# Revit family: EdgeProtection_FloorTransition_Schluter_Deco_AE
name_source: partatom
category: Profiles
units: mm (PartAtom-declared; Revit-internal decimal feet)

## family parameters
Classification Number = 23.35.50.11.21.17
Profile Usage = <Generic>
Rotate with component = No
Section Shape = Not Defined

## types (3) — shared parameters
Assembly Code = C3020430
Construction Details = http://www.arcat.com
Description = As Specified in 09 30 00
Green Building-LEED = http://www.arcat.com
Installation-Fabrication = http://www.schluter.com
Keynote = 09 30 00
Manufacturer = Schluter System LP
Manufacturer Fax = 800-477-9783
Manufacturer Website = http://www.schluter.com
Model = As Specified in 09 30 00
Product Data = http://www.arcat.com
Product Properties = http://www.arcat.com
Sales Information = http://www.schluter.com
Send Message = http://www.arcat.com
SpecWizard = http://www.arcat.com
Specification = http://www.arcat.com
Test Data = http://www.schluter.com
URL = http://www.schluter.com
zero-valued in all types: Expected Lifespan (Years), Maintenance Schedule (Months), Warranty Duration (Years)

## type names (no varying parameters)
- .5in
- .375in
- .3125in

## geometry (parser evidence)
native form markers: Sweep x1
no freeform markers — native parametric forms only
